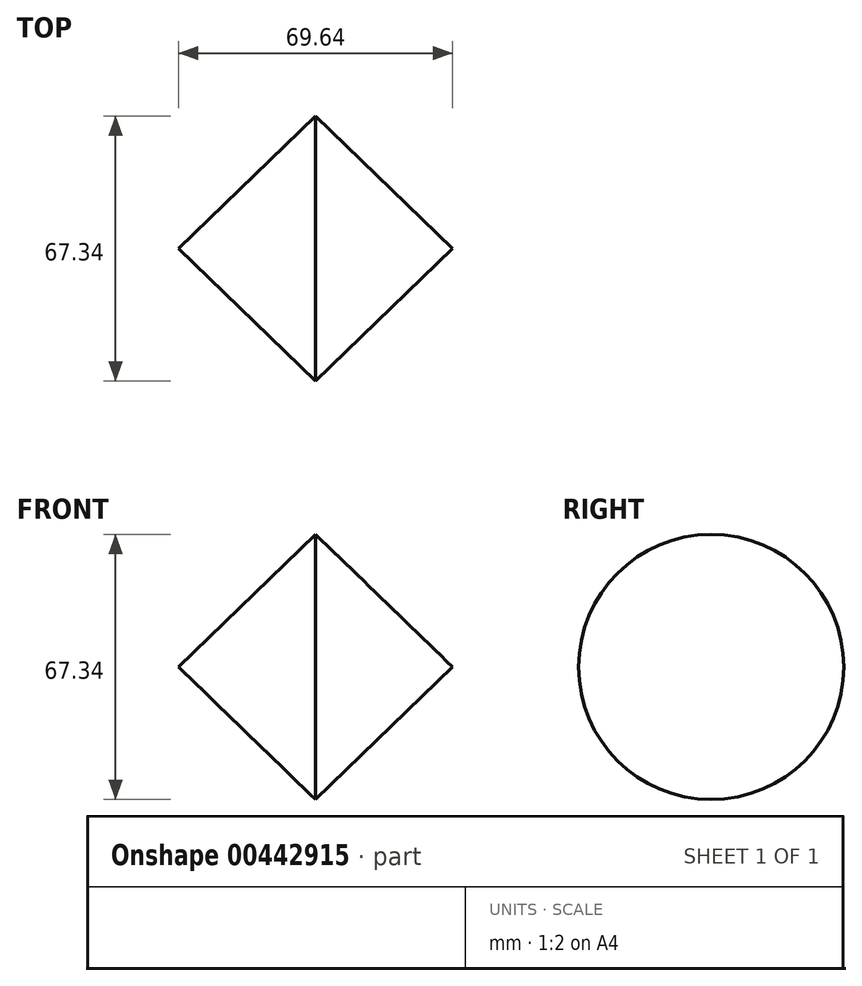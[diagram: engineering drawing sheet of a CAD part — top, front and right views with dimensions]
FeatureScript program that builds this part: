
annotation { "Feature Type Name" : "Feature", "Feature Type Description" : "" }
export const myFeature = defineFeature(function(context is Context, id is Id, definition is map)
    precondition{}
    {
        {
            var Q0;
            Q0=qCreatedBy(makeId("Front.planeOp"),FACE);
            var sketch = newSketch(context, id + "F0", { "sketchPlane" : qUnion([Q0])});
            skLineSegment(sketch, "E0", {"start": v(0, 33.67) * mm, "end": v(-34.82, 0) * mm});
            skLineSegment(sketch, "E1", {"start": v(-34.82, 0) * mm, "end": v(0, 0) * mm});
            skLineSegment(sketch, "E2.MirrorCS", {"start": v(0, 33.67) * mm, "end": v(34.82, 0) * mm});
            skLineSegment(sketch, "E3.MirrorCS", {"start": v(34.82, 0) * mm, "end": v(0, 0) * mm});
            skSolve(sketch);
        }
        {
            var Q0;
            Q0=makeQuery(id+"F0.imprint","IMPRINT",FACE,{"disambiguationData":[TD([[makeQuery(id+"F0.imprint","IMPRINT",EDGE,{"derivedFrom":sQuery(id+"F0.wireOp",EDGE,"E0")}),1.0]])]});
            var Q1;
            Q1=sQuery(id+"F0.wireOp",EDGE,"E1");
            revolve(context, id + "F1", {"entities" : qUnion([Q0]), "axis" : qUnion([Q1]), "revolveType" : RevolveType.FULL});
        }
    });
